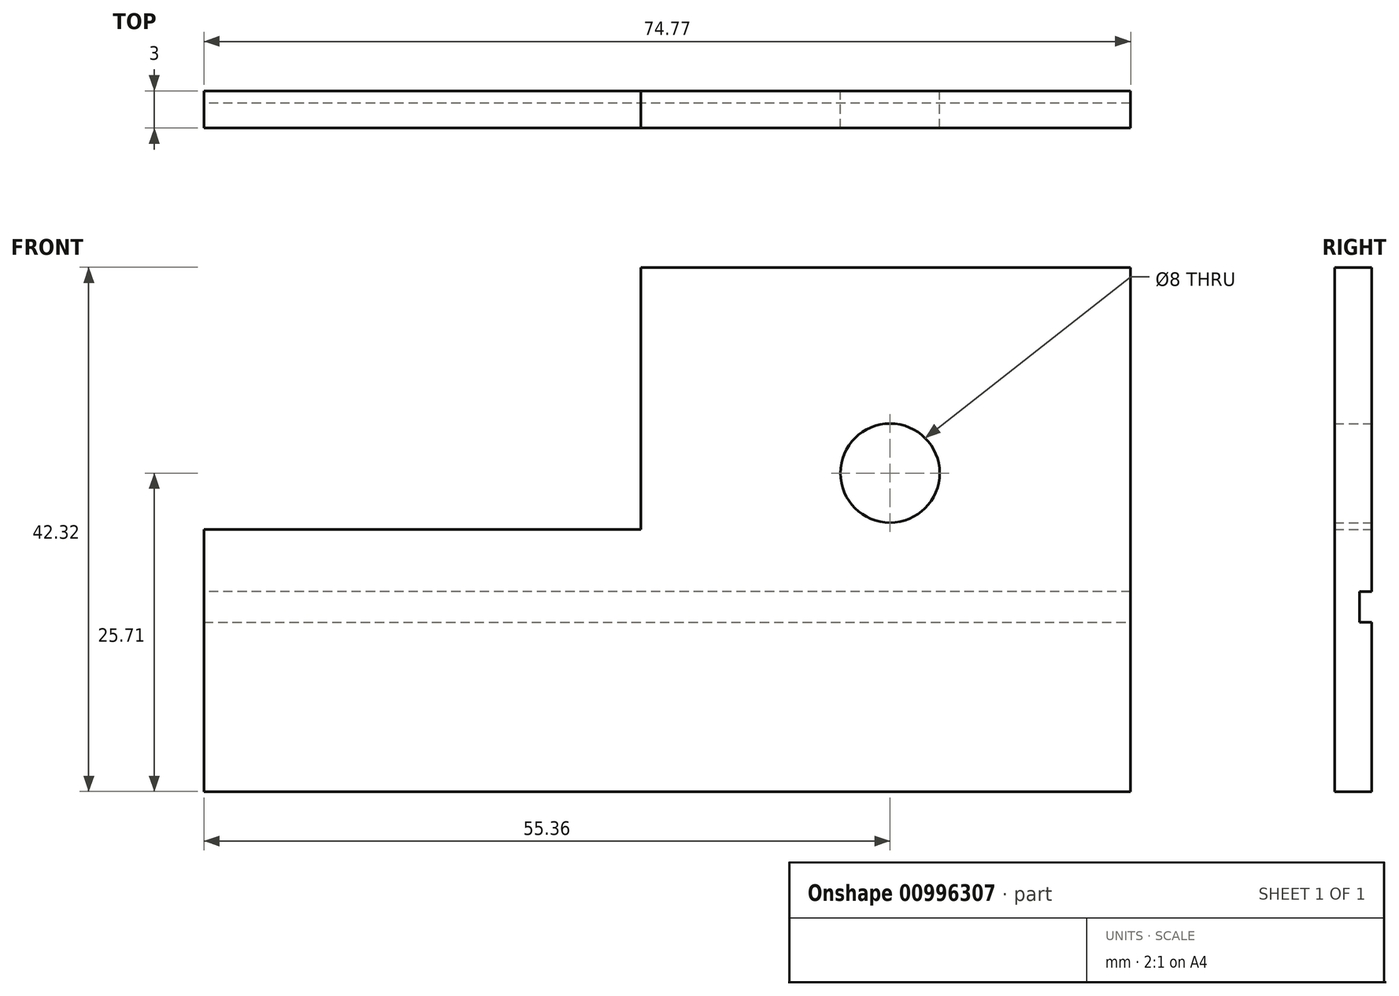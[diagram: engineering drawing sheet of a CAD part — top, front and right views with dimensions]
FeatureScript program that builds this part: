
annotation { "Feature Type Name" : "Feature", "Feature Type Description" : "" }
export const myFeature = defineFeature(function(context is Context, id is Id, definition is map)
    precondition{}
    {
        {
            var Q0;
            Q0=qCreatedBy(makeId("Front.planeOp"),FACE);
            var sketch = newSketch(context, id + "F0", { "sketchPlane" : qUnion([Q0])});
            skLineSegment(sketch, "E0.bottom", {"start": v(17.13, 16.6) * mm, "end": v(-14.73, 16.6) * mm});
            skLineSegment(sketch, "E0.top", {"start": v(17.13, -25.71) * mm, "end": v(-55.36, -25.71) * mm});
            skLineSegment(sketch, "E0.right", {"start": v(-55.36, -4.55) * mm, "end": v(-55.36, -25.71) * mm});
            skPoint(sketch, "E0.middle", {"position": v(-14.73, -4.55) * mm});
            skCircle(sketch, "E1", {"center": v(0, 0) * mm, "radius": 4 * mm});
            skLineSegment(sketch, "E2", {"start": v(-55.36, -4.55) * mm, "end": v(-20.12, -4.55) * mm});
            skLineSegment(sketch, "E3", {"start": v(17.13, 16.6) * mm, "end": v(19.4, 16.6) * mm});
            skLineSegment(sketch, "E4", {"start": v(19.4, 16.6) * mm, "end": v(19.4, -25.71) * mm});
            skLineSegment(sketch, "E5", {"start": v(17.13, -25.71) * mm, "end": v(19.4, -25.71) * mm});
            skLineSegment(sketch, "E6", {"start": v(-14.73, 16.6) * mm, "end": v(-20.12, 16.6) * mm});
            skLineSegment(sketch, "E7", {"start": v(-20.12, 16.6) * mm, "end": v(-20.12, -4.55) * mm});
            skSolve(sketch);
        }
        {
            var Q0;
            Q0=makeQuery(id+"F0.imprint","IMPRINT",FACE,{"disambiguationData":[TD([[makeQuery(id+"F0.imprint","IMPRINT",EDGE,{"derivedFrom":sQuery(id+"F0.wireOp",EDGE,"E0.bottom")}),1.0]])]});
            extrude(context, id + "F1", {"entities" : qUnion([Q0]), "depth" : 3 * mm, "offsetDistance" : 25 * mm});
        }
        {
            var Q0;
            Q0=makeQuery(id+"F1.opExtrude","CAP_FACE",FACE,{"disambiguationData":[OSD([sQuery(id+"F0.wireOp",EDGE,"E0.bottom"),sQuery(id+"F0.wireOp",EDGE,"E0.top"),sQuery(id+"F0.wireOp",EDGE,"E0.right"),sQuery(id+"F0.wireOp",EDGE,"E1"),sQuery(id+"F0.wireOp",EDGE,"E2"),sQuery(id+"F0.wireOp",EDGE,"E3"),sQuery(id+"F0.wireOp",EDGE,"E4"),sQuery(id+"F0.wireOp",EDGE,"E5"),sQuery(id+"F0.wireOp",EDGE,"E6"),sQuery(id+"F0.wireOp",EDGE,"E7")])],"isStart":true});
            var sketch = newSketch(context, id + "F2", { "sketchPlane" : qUnion([Q0])});
            skLineSegment(sketch, "E8", {"start": v(-19.4, -9.55) * mm, "end": v(55.36, -9.55) * mm});
            skLineSegment(sketch, "E9", {"start": v(55.36, -12.05) * mm, "end": v(-19.4, -12.05) * mm});
            skSolve(sketch);
        }
        {
            var Q0;
            {var subQ0=sQuery(id+"F2.wireOp",EDGE,"E8");Q0=makeQuery(id+"F2.imprint","IMPRINT",FACE,{"disambiguationData":[TD([[makeQuery(id+"F2.imprint","IMPRINT",EDGE,{"derivedFrom":subQ0}),-1.0]])]});}
            extrude(context, id + "F3", {"entities" : qUnion([Q0]), "operationType" : NewBodyOperationType.REMOVE, "oppositeDirection" : true, "depth" : 1 * mm, "offsetDistance" : 25 * mm});
        }
    });
